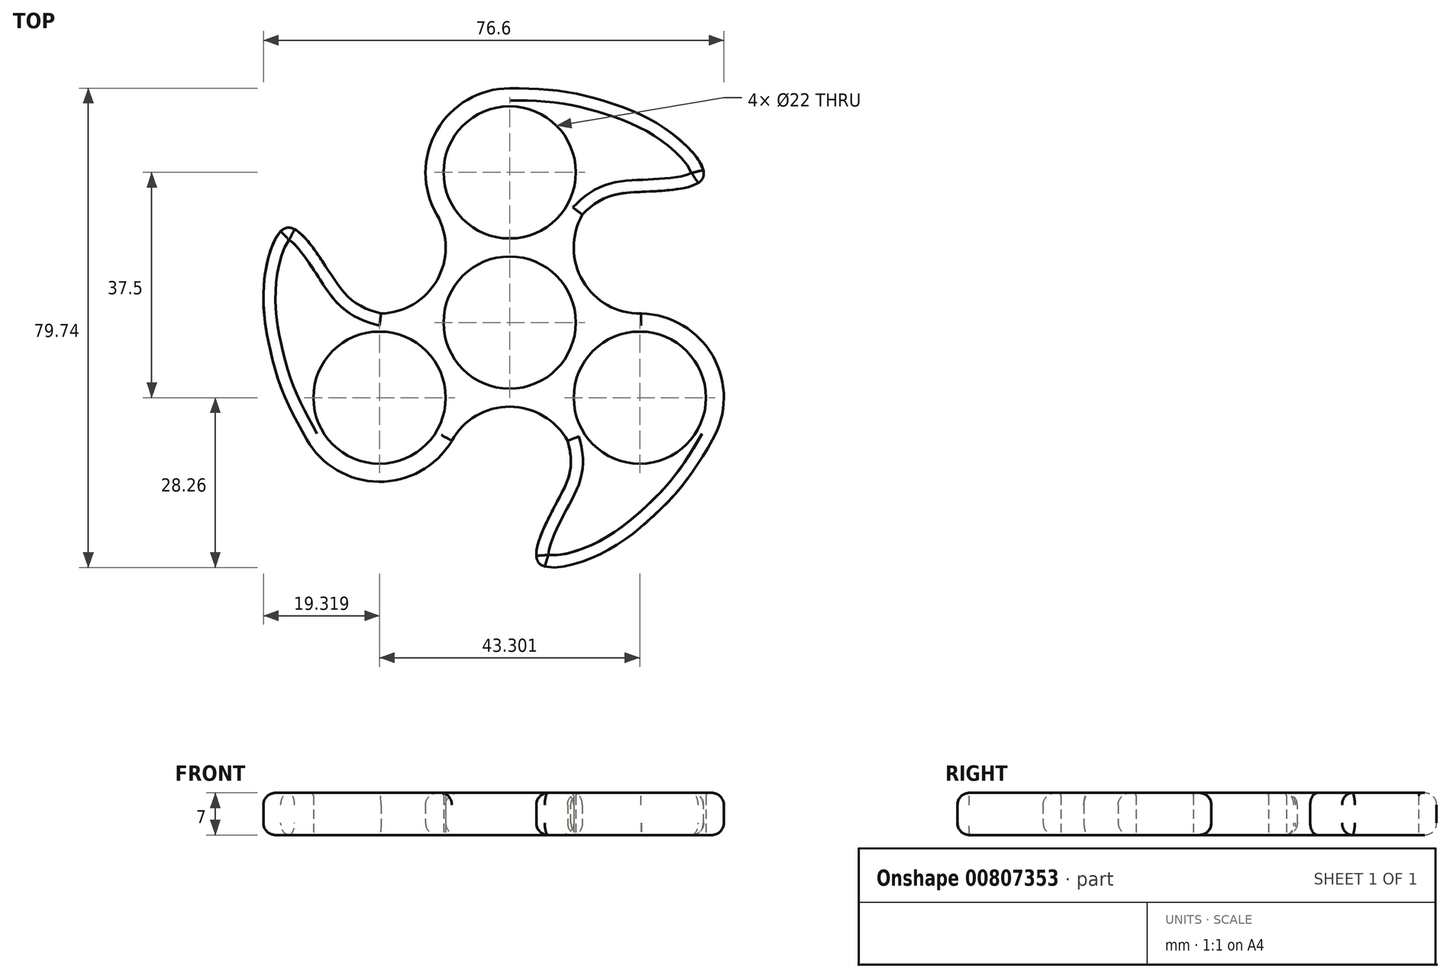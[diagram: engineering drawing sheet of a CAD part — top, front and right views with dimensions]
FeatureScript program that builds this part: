
annotation { "Feature Type Name" : "Feature", "Feature Type Description" : "" }
export const myFeature = defineFeature(function(context is Context, id is Id, definition is map)
    precondition{}
    {
        {
            var Q0;
            Q0=qCreatedBy(makeId("Top.planeOp"),FACE);
            var sketch = newSketch(context, id + "F0", { "sketchPlane" : qUnion([Q0])});
            skCircle(sketch, "E0", {"center": v(0, 0) * mm, "radius": 11 * mm});
            skCircle(sketch, "E1", {"center": v(0, 25) * mm, "radius": 11 * mm});
            skCircle(sketch, "E2.1.0", {"center": v(-21.65, -12.5) * mm, "radius": 11 * mm});
            skCircle(sketch, "E2.2.0", {"center": v(21.65, -12.5) * mm, "radius": 11 * mm});
            skArc(sketch, "E3", {"start": v(-24.93, -2) * mm, "mid": v(-31.17, -18) * mm, "end": v(-14.2, -20.58) * mm, "construction": true});
            skArc(sketch, "E4", {"start": v(14.19, -20.58) * mm, "mid": v(31.16, -18) * mm, "end": v(24.92, -2) * mm, "construction": true});
            skArc(sketch, "E5", {"start": v(10.73, 22.58) * mm, "mid": v(0, 35.98) * mm, "end": v(-10.73, 22.6) * mm});
            skArc(sketch, "E6", {"start": v(-9.64, -19.7) * mm, "mid": v(0, -14) * mm, "end": v(9.64, -19.7) * mm});
            skArc(sketch, "E7", {"start": v(21.88, 1.5) * mm, "mid": v(12.2, 6.87) * mm, "end": v(12.1, 17.95) * mm});
            skFitSpline(sketch, "E8", {"points": [v(0, 38.98) * mm, v(14.82, 37.12) * mm, v(26.3, 31.99) * mm, v(32.13, 24.04) * mm, v(21.46, 21.72) * mm, v(12.1, 17.95) * mm], "startDerivative": vector(103.34, -0.06) * mm, "endDerivative": vector(-52.51, -53.48) * mm});
            skArc(sketch, "E9", {"start": v(0, 38.98) * mm, "mid": v(-12.13, 31.96) * mm, "end": v(-12.1, 17.94) * mm});
            skFitSpline(sketch, "E10.MirrorCS", {"points": [v(-33.77, -19.46) * mm, v(-39.56, -5.72) * mm, v(-40.85, 6.78) * mm, v(-36.88, 15.81) * mm, v(-29.54, 7.73) * mm, v(-21.4, 1.5) * mm], "startDerivative": vector(-51.6, 89.54) * mm, "endDerivative": vector(72.56, -18.75) * mm});
            skFitSpline(sketch, "E11.MirrorCS", {"points": [v(33.75, -19.5) * mm, v(24.73, -31.4) * mm, v(14.55, -38.77) * mm, v(4.75, -39.85) * mm, v(8.08, -29.45) * mm, v(9.64, -19.7) * mm], "startDerivative": vector(-51.73, -89.46) * mm, "endDerivative": vector(-20.05, 72.22) * mm});
            skArc(sketch, "E12", {"start": v(33.75, -19.5) * mm, "mid": v(33.82, -5.6) * mm, "end": v(21.88, 1.5) * mm});
            skArc(sketch, "E13", {"start": v(-33.77, -19.46) * mm, "mid": v(-21.78, -26.48) * mm, "end": v(-9.64, -19.7) * mm});
            skArc(sketch, "E14", {"start": v(-21.4, 1.5) * mm, "mid": v(-12.08, 7.07) * mm, "end": v(-12.1, 17.94) * mm});
            skSolve(sketch);
        }
        {
            var Q0;
            Q0=makeQuery(id+"F0.imprint","IMPRINT",FACE,{"disambiguationData":[TD([[makeQuery(id+"F0.imprint","IMPRINT",EDGE,{"derivedFrom":sQuery(id+"F0.wireOp",EDGE,"E0")}),-1.0]])]});
            extrude(context, id + "F1", {"entities" : qUnion([Q0]), "depth" : 7 * mm, "offsetDistance" : 25 * mm});
        }
        {
            var Q0;
            Q0=makeQuery(id+"F1.opExtrude","CAP_EDGE",EDGE,{"disambiguationData":[OSD([sQuery(id+"F0.wireOp",EDGE,"E14")])],"isStart":false});
            var Q1;
            Q1=makeQuery(id+"F1.opExtrude","CAP_EDGE",EDGE,{"disambiguationData":[OSD([sQuery(id+"F0.wireOp",EDGE,"E7")])],"isStart":false});
            var Q2;
            Q2=makeQuery(id+"F1.opExtrude","CAP_EDGE",EDGE,{"disambiguationData":[OSD([sQuery(id+"F0.wireOp",EDGE,"E6")])],"isStart":false});
            fillet(context, id + "F2", {"entities" : qUnion([Q0, Q1, Q2]), "radius" : 2 * mm, "tangentPropagation" : true, "allowEdgeOverflow" : false});
        }
        {
            var Q0;
            Q0=makeQuery(id+"F1.opExtrude","CAP_EDGE",EDGE,{"disambiguationData":[OSD([sQuery(id+"F0.wireOp",EDGE,"E8")])],"isStart":false});
            var Q1;
            Q1=makeQuery(id+"F1.opExtrude","CAP_EDGE",EDGE,{"disambiguationData":[OSD([sQuery(id+"F0.wireOp",EDGE,"E10.MirrorCS")])],"isStart":false});
            var Q2;
            Q2=makeQuery(id+"F1.opExtrude","CAP_EDGE",EDGE,{"disambiguationData":[OSD([sQuery(id+"F0.wireOp",EDGE,"E11.MirrorCS"),sQuery(id+"F0.wireOp",EDGE,"E11.MirrorCS")])],"isStart":false});
            var Q3;
            Q3=makeQuery(id+"F1.opExtrude","CAP_EDGE",EDGE,{"disambiguationData":[OSD([sQuery(id+"F0.wireOp",EDGE,"E12")])],"isStart":false});
            var Q4;
            Q4=makeQuery(id+"F1.opExtrude","CAP_EDGE",EDGE,{"disambiguationData":[OSD([sQuery(id+"F0.wireOp",EDGE,"E13")])],"isStart":false});
            var Q5;
            Q5=makeQuery(id+"F1.opExtrude","CAP_EDGE",EDGE,{"disambiguationData":[OSD([sQuery(id+"F0.wireOp",EDGE,"E9")])],"isStart":false});
            fillet(context, id + "F3", {"entities" : qUnion([Q0, Q1, Q2, Q3, Q4, Q5]), "radius" : 2 * mm, "tangentPropagation" : true, "allowEdgeOverflow" : false});
        }
        {
            var Q0;
            Q0=makeQuery(id+"F1.opExtrude","CAP_EDGE",EDGE,{"disambiguationData":[OSD([sQuery(id+"F0.wireOp",EDGE,"E6")])],"isStart":true});
            var Q1;
            Q1=makeQuery(id+"F1.opExtrude","CAP_EDGE",EDGE,{"disambiguationData":[OSD([sQuery(id+"F0.wireOp",EDGE,"E7")])],"isStart":true});
            var Q2;
            Q2=makeQuery(id+"F1.opExtrude","CAP_EDGE",EDGE,{"disambiguationData":[OSD([sQuery(id+"F0.wireOp",EDGE,"E14")])],"isStart":true});
            var Q3;
            Q3=makeQuery(id+"F1.opExtrude","CAP_EDGE",EDGE,{"disambiguationData":[OSD([sQuery(id+"F0.wireOp",EDGE,"E8")])],"isStart":true});
            var Q4;
            Q4=makeQuery(id+"F1.opExtrude","CAP_EDGE",EDGE,{"disambiguationData":[OSD([sQuery(id+"F0.wireOp",EDGE,"E9")])],"isStart":true});
            var Q5;
            Q5=makeQuery(id+"F1.opExtrude","CAP_EDGE",EDGE,{"disambiguationData":[OSD([sQuery(id+"F0.wireOp",EDGE,"E10.MirrorCS")])],"isStart":true});
            var Q6;
            Q6=makeQuery(id+"F1.opExtrude","CAP_EDGE",EDGE,{"disambiguationData":[OSD([sQuery(id+"F0.wireOp",EDGE,"E13")])],"isStart":true});
            var Q7;
            Q7=makeQuery(id+"F1.opExtrude","CAP_EDGE",EDGE,{"disambiguationData":[OSD([sQuery(id+"F0.wireOp",EDGE,"E11.MirrorCS"),sQuery(id+"F0.wireOp",EDGE,"E11.MirrorCS")])],"isStart":true});
            var Q8;
            Q8=makeQuery(id+"F1.opExtrude","CAP_EDGE",EDGE,{"disambiguationData":[OSD([sQuery(id+"F0.wireOp",EDGE,"E12")])],"isStart":true});
            fillet(context, id + "F4", {"entities" : qUnion([Q0, Q1, Q2, Q3, Q4, Q5, Q6, Q7, Q8]), "radius" : 2 * mm, "tangentPropagation" : true, "allowEdgeOverflow" : false});
        }
        {
            var Q0;
            Q0=makeQuery(id+"F1.opExtrude","CAP_EDGE",EDGE,{"disambiguationData":[OSD([sQuery(id+"F0.wireOp",EDGE,"E1")])],"isStart":false});
            var Q1;
            Q1=makeQuery(id+"F1.opExtrude","CAP_EDGE",EDGE,{"disambiguationData":[OSD([sQuery(id+"F0.wireOp",EDGE,"E0")])],"isStart":false});
            var Q2;
            Q2=makeQuery(id+"F1.opExtrude","CAP_EDGE",EDGE,{"disambiguationData":[OSD([sQuery(id+"F0.wireOp",EDGE,"E2.2.0")])],"isStart":false});
            var Q3;
            Q3=makeQuery(id+"F1.opExtrude","CAP_EDGE",EDGE,{"disambiguationData":[OSD([sQuery(id+"F0.wireOp",EDGE,"E2.1.0")])],"isStart":false});
            fillet(context, id + "F5", {"entities" : qUnion([Q0, Q1, Q2, Q3]), "radius" : 0.5 * mm, "tangentPropagation" : true, "allowEdgeOverflow" : false});
        }
    });
